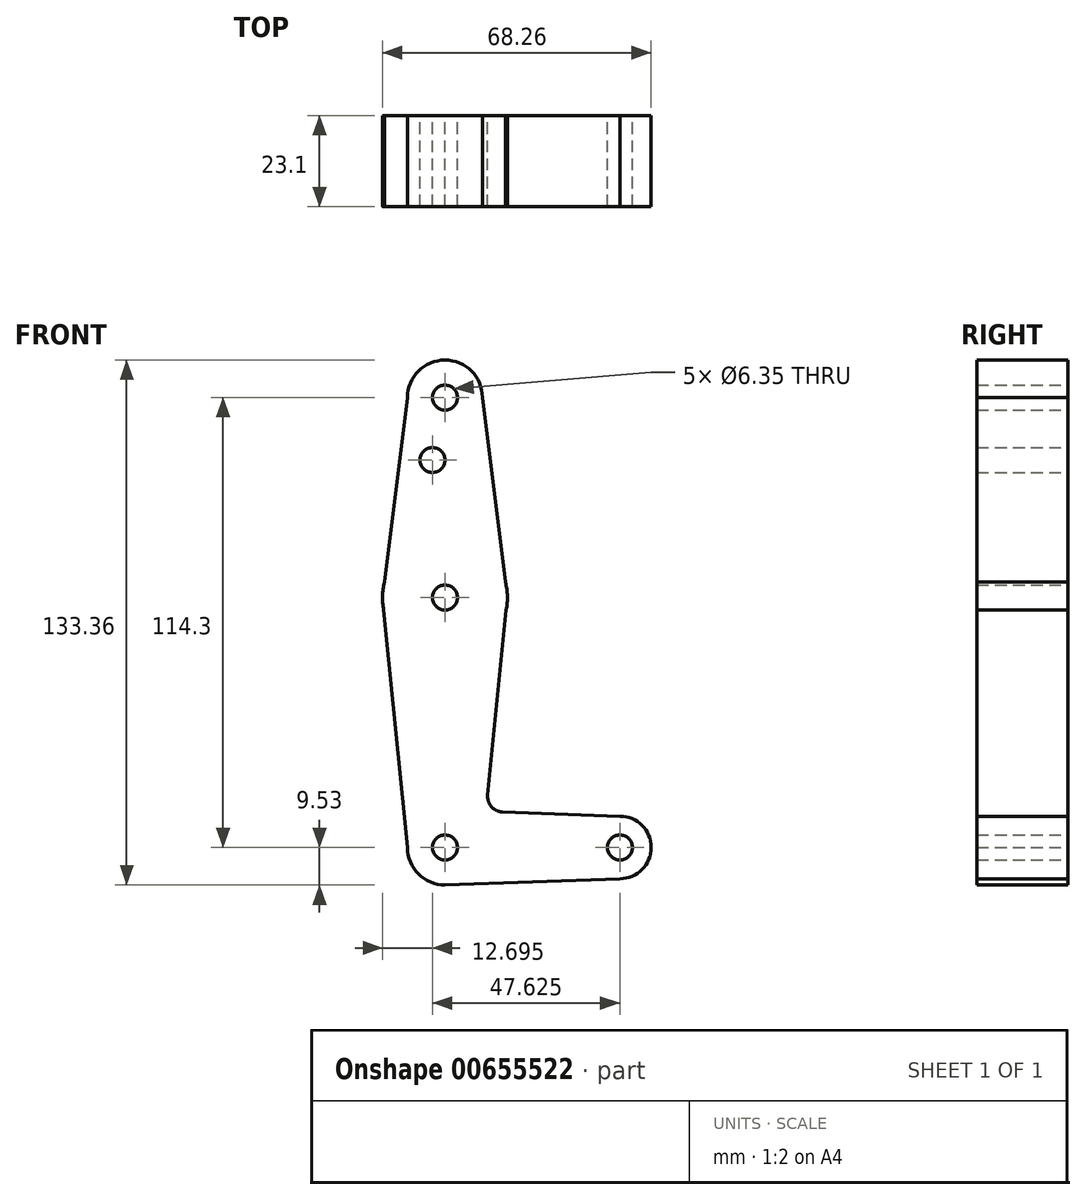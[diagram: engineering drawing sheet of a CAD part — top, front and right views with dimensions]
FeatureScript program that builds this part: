
annotation { "Feature Type Name" : "Feature", "Feature Type Description" : "" }
export const myFeature = defineFeature(function(context is Context, id is Id, definition is map)
    precondition{}
    {
        {
            var Q0;
            Q0=qCreatedBy(makeId("Front.planeOp"),FACE);
            var sketch = newSketch(context, id + "F0", { "sketchPlane" : qUnion([Q0])});
            skLineSegment(sketch, "E0", {"start": v(0, 0) * mm, "end": v(44.45, 0) * mm});
            skLineSegment(sketch, "E1", {"start": v(0, 0) * mm, "end": v(0, 63.5) * mm});
            skLineSegment(sketch, "E2", {"start": v(0, 63.5) * mm, "end": v(0, 114.3) * mm});
            skCircle(sketch, "E3", {"center": v(0, 114.3) * mm, "radius": 9.53 * mm});
            skCircle(sketch, "E4", {"center": v(0, 63.5) * mm, "radius": 15.88 * mm});
            skCircle(sketch, "E5", {"center": v(0, 0) * mm, "radius": 9.53 * mm});
            skCircle(sketch, "E6", {"center": v(44.45, 0) * mm, "radius": 7.94 * mm});
            skLineSegment(sketch, "E7", {"start": v(-9.52, 114.3) * mm, "end": v(-15.88, 63.5) * mm});
            skLineSegment(sketch, "E8", {"start": v(-15.88, 63.5) * mm, "end": v(-9.52, 0) * mm});
            skLineSegment(sketch, "E9", {"start": v(9.52, 0) * mm, "end": v(15.88, 63.5) * mm});
            skLineSegment(sketch, "E10", {"start": v(15.88, 63.5) * mm, "end": v(9.52, 114.3) * mm});
            skLineSegment(sketch, "E11", {"start": v(0, -9.52) * mm, "end": v(44.45, -7.94) * mm});
            skLineSegment(sketch, "E12", {"start": v(0, 9.52) * mm, "end": v(44.45, 7.94) * mm});
            skCircle(sketch, "E13", {"center": v(-3.18, 98.44) * mm, "radius": 3.18 * mm});
            skCircle(sketch, "E14", {"center": v(0, 114.3) * mm, "radius": 3.18 * mm});
            skCircle(sketch, "E15", {"center": v(0, 63.5) * mm, "radius": 3.18 * mm});
            skCircle(sketch, "E16", {"center": v(0, 0) * mm, "radius": 3.18 * mm});
            skCircle(sketch, "E17", {"center": v(44.45, 0) * mm, "radius": 3.18 * mm});
            skCircle(sketch, "E18", {"center": v(14.82, 12.97) * mm, "radius": 3.98 * mm});
            skPoint(sketch, "E18.first.point", {"position": v(10.86, 13.37) * mm});
            skPoint(sketch, "E18.second.point", {"position": v(14.68, 9) * mm});
            skPoint(sketch, "E18.third.point", {"position": v(17.87, 15.52) * mm});
            skSolve(sketch);
        }
        {
            var Q0;
            {var subQ1=sQuery(id+"F0.wireOp",EDGE,"E0");var subQ5=sQuery(id+"F0.wireOp",EDGE,"E16");var subQ6=makeQuery(id+"F0.imprint","INTERSECT",VERTEX,{"derivedFrom":[subQ1,subQ5]});Q0=makeQuery(id+"F0.imprint","IMPRINT",FACE,{"disambiguationData":[TD([[makeQuery(id+"F0.imprint","IMPRINT",EDGE,{"disambiguationData":[TD([[subQ6,-1.0]])],"derivedFrom":subQ5}),-1.0]])]});}
            var Q1;
            {var subQ3=sQuery(id+"F0.wireOp",EDGE,"E2");var subQ8=makeQuery(id+"F0.imprint","INTERSECT",VERTEX,{"derivedFrom":[subQ3,sQuery(id+"F0.wireOp",EDGE,"E13")]});Q1=makeQuery(id+"F0.imprint","IMPRINT",FACE,{"disambiguationData":[TD([[makeQuery(id+"F0.imprint","IMPRINT",EDGE,{"disambiguationData":[TD([[subQ8,1.0]])],"derivedFrom":subQ3}),-1.0]])]});}
            var Q2;
            {var subQ1=sQuery(id+"F0.wireOp",EDGE,"E5");var subQ3=sQuery(id+"F0.wireOp",EDGE,"E12");var subQ4=makeQuery(id+"F0.imprint","INTERSECT",VERTEX,{"derivedFrom":[subQ1,subQ3]});Q2=makeQuery(id+"F0.imprint","IMPRINT",FACE,{"disambiguationData":[TD([[makeQuery(id+"F0.imprint","IMPRINT",EDGE,{"disambiguationData":[TD([[subQ4,-1.0]])],"derivedFrom":subQ3}),-1.0]])]});}
            var Q3;
            {var subQ0=sQuery(id+"F0.wireOp",EDGE,"E5");var subQ1=makeQuery(id+"F0.imprint","INTERSECT",VERTEX,{"derivedFrom":[subQ0,sQuery(id+"F0.wireOp",EDGE,"E8")]});Q3=makeQuery(id+"F0.imprint","IMPRINT",FACE,{"disambiguationData":[TD([[makeQuery(id+"F0.imprint","IMPRINT",EDGE,{"disambiguationData":[TD([[subQ1,-1.0]])],"derivedFrom":subQ0}),1.0]])]});}
            var Q4;
            {var subQ0=sQuery(id+"F0.wireOp",EDGE,"E12");var subQ6=sQuery(id+"F0.wireOp",EDGE,"E6");var subQ8=makeQuery(id+"F0.imprint","INTERSECT",VERTEX,{"derivedFrom":[subQ6,subQ0]});Q4=makeQuery(id+"F0.imprint","IMPRINT",FACE,{"disambiguationData":[TD([[makeQuery(id+"F0.imprint","IMPRINT",EDGE,{"disambiguationData":[TD([[subQ8,-1.0]])],"derivedFrom":subQ6}),-1.0]])]});}
            var Q5;
            Q5=makeQuery(id+"F0.imprint","IMPRINT",FACE,{"disambiguationData":[TD([[makeQuery(id+"F0.imprint","IMPRINT",EDGE,{"derivedFrom":sQuery(id+"F0.wireOp",EDGE,"E17")}),-1.0]])]});
            var Q6;
            {var subQ3=sQuery(id+"F0.wireOp",EDGE,"E4");var subQ5=sQuery(id+"F0.wireOp",EDGE,"E8");var subQ6=makeQuery(id+"F0.imprint","INTERSECT",VERTEX,{"derivedFrom":[subQ3,subQ5]});Q6=makeQuery(id+"F0.imprint","IMPRINT",FACE,{"disambiguationData":[TD([[makeQuery(id+"F0.imprint","IMPRINT",EDGE,{"disambiguationData":[TD([[subQ6,-1.0]])],"derivedFrom":subQ3}),-1.0]])]});}
            var Q7;
            {var subQ1=sQuery(id+"F0.wireOp",EDGE,"E4");var subQ3=sQuery(id+"F0.wireOp",EDGE,"E1");var subQ4=makeQuery(id+"F0.imprint","INTERSECT",VERTEX,{"derivedFrom":[subQ3,subQ1]});Q7=makeQuery(id+"F0.imprint","IMPRINT",FACE,{"disambiguationData":[TD([[makeQuery(id+"F0.imprint","IMPRINT",EDGE,{"disambiguationData":[TD([[subQ4,-1.0]])],"derivedFrom":subQ3}),1.0]])]});}
            var Q8;
            {var subQ3=sQuery(id+"F0.wireOp",EDGE,"E6");var subQ5=sQuery(id+"F0.wireOp",EDGE,"E11");var subQ7=makeQuery(id+"F0.imprint","INTERSECT",VERTEX,{"derivedFrom":[subQ3,subQ5]});Q8=makeQuery(id+"F0.imprint","IMPRINT",FACE,{"disambiguationData":[TD([[makeQuery(id+"F0.imprint","IMPRINT",EDGE,{"disambiguationData":[TD([[subQ7,1.0]])],"derivedFrom":subQ3}),-1.0]])]});}
            var Q9;
            {var subQ3=sQuery(id+"F0.wireOp",EDGE,"E4");var subQ7=sQuery(id+"F0.wireOp",EDGE,"E1");var subQ8=makeQuery(id+"F0.imprint","INTERSECT",VERTEX,{"derivedFrom":[subQ7,subQ3]});Q9=makeQuery(id+"F0.imprint","IMPRINT",FACE,{"disambiguationData":[TD([[makeQuery(id+"F0.imprint","IMPRINT",EDGE,{"disambiguationData":[TD([[subQ8,-1.0]])],"derivedFrom":subQ7}),-1.0]])]});}
            var Q10;
            {var subQ8=sQuery(id+"F0.wireOp",EDGE,"E13");Q10=makeQuery(id+"F0.imprint","IMPRINT",FACE,{"disambiguationData":[TD([[makeQuery(id+"F0.imprint","IMPRINT",EDGE,{"derivedFrom":subQ8}),-1.0]])]});}
            var Q11;
            {var subQ0=sQuery(id+"F0.wireOp",EDGE,"E9");var subQ8=sQuery(id+"F0.wireOp",EDGE,"E4");var subQ9=makeQuery(id+"F0.imprint","INTERSECT",VERTEX,{"derivedFrom":[subQ8,subQ0]});Q11=makeQuery(id+"F0.imprint","IMPRINT",FACE,{"disambiguationData":[TD([[makeQuery(id+"F0.imprint","IMPRINT",EDGE,{"disambiguationData":[TD([[subQ9,1.0]])],"derivedFrom":subQ8}),-1.0]])]});}
            var Q12;
            Q12=makeQuery(id+"F0.imprint","IMPRINT",FACE,{"disambiguationData":[TD([[makeQuery(id+"F0.imprint","IMPRINT",EDGE,{"derivedFrom":sQuery(id+"F0.wireOp",EDGE,"E14")}),-1.0]])]});
            var Q13;
            {var subQ0=sQuery(id+"F0.wireOp",EDGE,"E9");var subQ1=sQuery(id+"F0.wireOp",EDGE,"E4");var subQ3=makeQuery(id+"F0.imprint","INTERSECT",VERTEX,{"derivedFrom":[subQ1,subQ0]});Q13=makeQuery(id+"F0.imprint","IMPRINT",FACE,{"disambiguationData":[TD([[makeQuery(id+"F0.imprint","IMPRINT",EDGE,{"disambiguationData":[TD([[subQ3,-1.0]])],"derivedFrom":subQ1}),1.0]])]});}
            var Q14;
            {var subQ0=sQuery(id+"F0.wireOp",EDGE,"E12");var subQ1=sQuery(id+"F0.wireOp",EDGE,"E5");var subQ3=makeQuery(id+"F0.imprint","INTERSECT",VERTEX,{"derivedFrom":[subQ1,subQ0]});Q14=makeQuery(id+"F0.imprint","IMPRINT",FACE,{"disambiguationData":[TD([[makeQuery(id+"F0.imprint","IMPRINT",EDGE,{"disambiguationData":[TD([[subQ3,-1.0]])],"derivedFrom":subQ1}),1.0]])]});}
            var Q15;
            {var subQ0=sQuery(id+"F0.wireOp",EDGE,"E11");var subQ1=sQuery(id+"F0.wireOp",EDGE,"E5");var subQ2=makeQuery(id+"F0.imprint","INTERSECT",VERTEX,{"disambiguationData":[OD(0.0)],"derivedFrom":[subQ1,subQ0]});Q15=makeQuery(id+"F0.imprint","IMPRINT",FACE,{"disambiguationData":[TD([[makeQuery(id+"F0.imprint","IMPRINT",EDGE,{"disambiguationData":[TD([[subQ2,-1.0]])],"derivedFrom":subQ1}),1.0]])]});}
            var Q16;
            {var subQ0=sQuery(id+"F0.wireOp",EDGE,"E18");var subQ1=sQuery(id+"F0.wireOp",EDGE,"E9");var subQ2=makeQuery(id+"F0.imprint","INTERSECT",VERTEX,{"derivedFrom":[subQ1,subQ0]});Q16=makeQuery(id+"F0.imprint","IMPRINT",FACE,{"disambiguationData":[TD([[makeQuery(id+"F0.imprint","IMPRINT",EDGE,{"disambiguationData":[TD([[subQ2,1.0]])],"derivedFrom":subQ1}),-1.0]])]});}
            var Q17;
            {var subQ0=sQuery(id+"F0.wireOp",EDGE,"E10");var subQ1=sQuery(id+"F0.wireOp",EDGE,"E4");var subQ3=makeQuery(id+"F0.imprint","INTERSECT",VERTEX,{"derivedFrom":[subQ1,subQ0]});Q17=makeQuery(id+"F0.imprint","IMPRINT",FACE,{"disambiguationData":[TD([[makeQuery(id+"F0.imprint","IMPRINT",EDGE,{"disambiguationData":[TD([[subQ3,1.0]])],"derivedFrom":subQ1}),1.0]])]});}
            var Q18;
            {var subQ0=sQuery(id+"F0.wireOp",EDGE,"E7");var subQ1=sQuery(id+"F0.wireOp",EDGE,"E4");var subQ3=makeQuery(id+"F0.imprint","INTERSECT",VERTEX,{"derivedFrom":[subQ1,subQ0]});Q18=makeQuery(id+"F0.imprint","IMPRINT",FACE,{"disambiguationData":[TD([[makeQuery(id+"F0.imprint","IMPRINT",EDGE,{"disambiguationData":[TD([[subQ3,-1.0]])],"derivedFrom":subQ1}),1.0]])]});}
            var Q19;
            {var subQ0=sQuery(id+"F0.wireOp",EDGE,"E8");var subQ1=sQuery(id+"F0.wireOp",EDGE,"E4");var subQ3=makeQuery(id+"F0.imprint","INTERSECT",VERTEX,{"derivedFrom":[subQ1,subQ0]});Q19=makeQuery(id+"F0.imprint","IMPRINT",FACE,{"disambiguationData":[TD([[makeQuery(id+"F0.imprint","IMPRINT",EDGE,{"disambiguationData":[TD([[subQ3,1.0]])],"derivedFrom":subQ1}),1.0]])]});}
            extrude(context, id + "F1", {"entities" : qUnion([Q0, Q1, Q2, Q3, Q4, Q5, Q6, Q7, Q8, Q9, Q10, Q11, Q12, Q13, Q14, Q15, Q16, Q17, Q18, Q19]), "depth" : 23.1 * mm, "offsetDistance" : 25 * mm});
        }
    });
